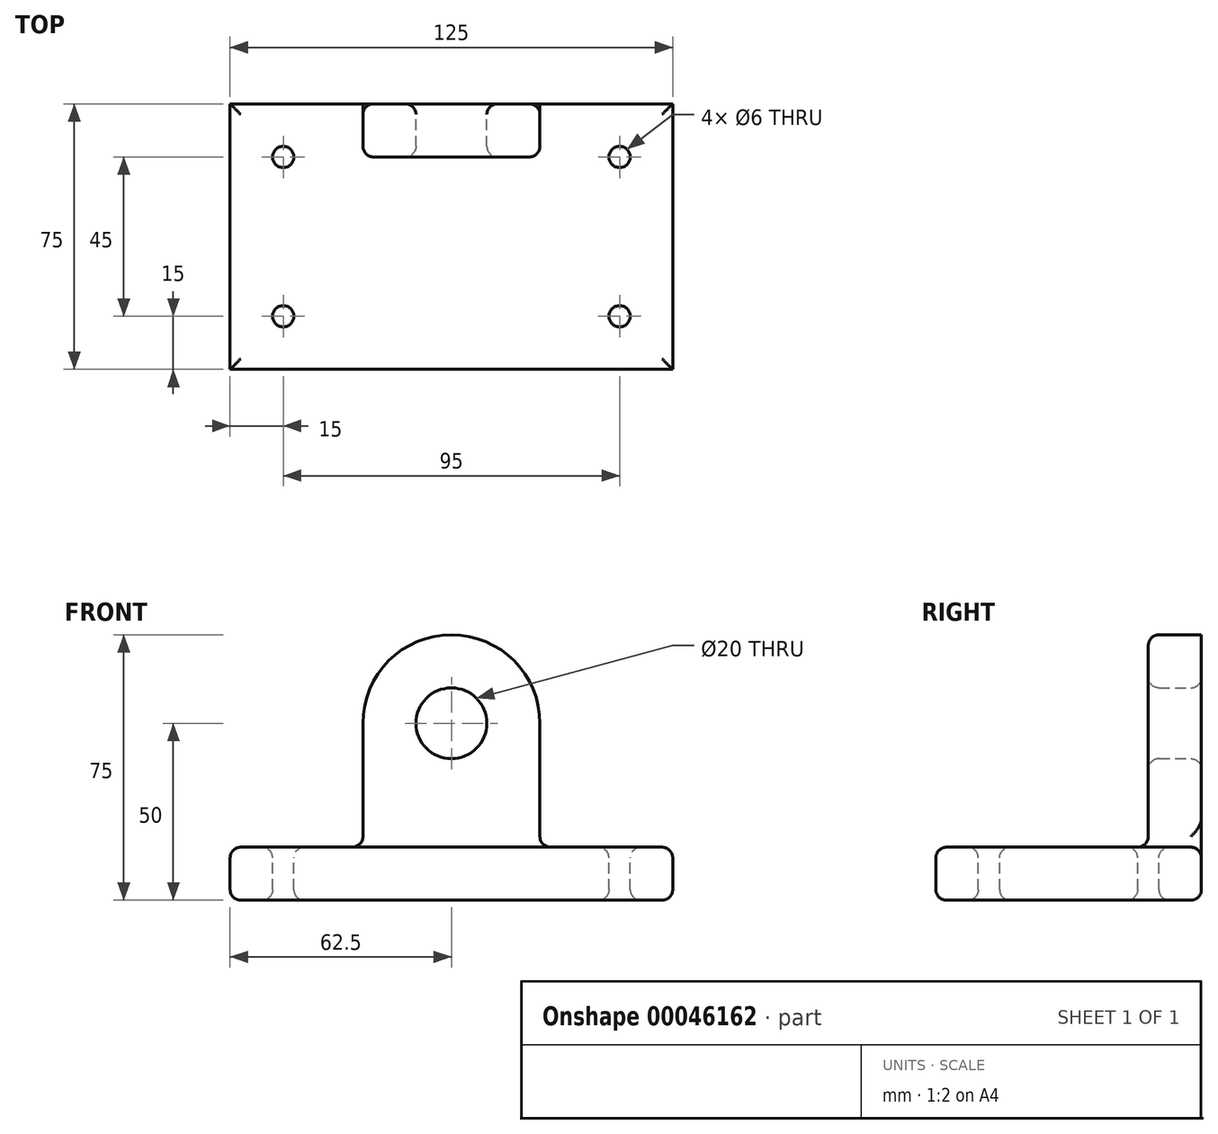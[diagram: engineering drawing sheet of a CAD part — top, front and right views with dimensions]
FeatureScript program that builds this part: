
annotation { "Feature Type Name" : "Feature", "Feature Type Description" : "" }
export const myFeature = defineFeature(function(context is Context, id is Id, definition is map)
    precondition{}
    {
        {
            var Q0;
            Q0=qCreatedBy(makeId("Top.planeOp"),FACE);
            var sketch = newSketch(context, id + "F0", { "sketchPlane" : qUnion([Q0])});
            skLineSegment(sketch, "E0.rect.bottom", {"start": v(62.5, 37.5) * mm, "end": v(-62.5, 37.5) * mm});
            skLineSegment(sketch, "E0.rect.top", {"start": v(62.5, -37.5) * mm, "end": v(-62.5, -37.5) * mm});
            skLineSegment(sketch, "E0.rect.left", {"start": v(62.5, 37.5) * mm, "end": v(62.5, -37.5) * mm});
            skLineSegment(sketch, "E0.rect.right", {"start": v(-62.5, 37.5) * mm, "end": v(-62.5, -37.5) * mm});
            skPoint(sketch, "E0.rect.middle", {"position": v(0, 0) * mm});
            skSolve(sketch);
        }
        {
            var Q0;
            Q0 = qSketchRegion(id + "F0", true);
            extrude(context, id + "F1", {"entities" : qUnion([Q0]), "depth" : 15 * mm});
        }
        {
            var Q0;
            Q0=makeQuery(id+"F1.opExtrude","SWEPT_FACE",FACE,{"disambiguationData":[OSD([sQuery(id+"F0.wireOp",EDGE,"E0.rect.bottom")])]});
            var sketch = newSketch(context, id + "F2", { "sketchPlane" : qUnion([Q0])});
            skLineSegment(sketch, "E1", {"start": v(0, 0) * mm, "end": v(0, 50) * mm, "construction": true});
            skCircle(sketch, "E2", {"center": v(0, 50) * mm, "radius": 25 * mm});
            skLineSegment(sketch, "E3.bottom", {"start": v(-25, 50) * mm, "end": v(25, 50) * mm});
            skLineSegment(sketch, "E3.top", {"start": v(-25, 0) * mm, "end": v(25, 0) * mm});
            skLineSegment(sketch, "E3.left", {"start": v(-25, 50) * mm, "end": v(-25, 0) * mm});
            skLineSegment(sketch, "E3.right", {"start": v(25, 50) * mm, "end": v(25, 0) * mm});
            skCircle(sketch, "E4", {"center": v(0, 50) * mm, "radius": 10 * mm});
            skSolve(sketch);
        }
        {
            var Q0;
            {var subQ0=sQuery(id+"F2.wireOp",EDGE,"E3.bottom");Q0=makeQuery(id+"F2.imprint","IMPRINT",FACE,{"disambiguationData":[TD([[makeQuery(id+"F2.imprint","IMPRINT",EDGE,{"derivedFrom":subQ0}),1.0]])]});}
            var Q1;
            {var subQ0=sQuery(id+"F2.wireOp",EDGE,"E3.bottom");Q1=makeQuery(id+"F2.imprint","IMPRINT",FACE,{"disambiguationData":[TD([[makeQuery(id+"F2.imprint","IMPRINT",EDGE,{"derivedFrom":subQ0}),-1.0]])]});}
            var Q2;
            {var subQ0=makeQuery(id+"F1.opExtrude","CAP_EDGE",EDGE,{"disambiguationData":[OSD([sQuery(id+"F0.wireOp",EDGE,"E0.rect.bottom")])],"isStart":false});var subQ3=sQuery(id+"F2.wireOp",EDGE,"E3.left");var subQ4=makeQuery(id+"F2.imprint","INTERSECT",VERTEX,{"derivedFrom":[subQ0,subQ3]});Q2=makeQuery(id+"F2.imprint","IMPRINT",FACE,{"disambiguationData":[TD([[makeQuery(id+"F2.imprint","IMPRINT",EDGE,{"disambiguationData":[TD([[subQ4,-1.0]])],"derivedFrom":subQ0}),1.0]])]});}
            var Q3;
            {var subQ7=sQuery(id+"F2.wireOp",EDGE,"E3.top");Q3=makeQuery(id+"F2.imprint","IMPRINT",FACE,{"disambiguationData":[TD([[makeQuery(id+"F2.imprint","IMPRINT",EDGE,{"derivedFrom":subQ7}),1.0]])]});}
            extrude(context, id + "F3", {"entities" : qUnion([Q0, Q1, Q2, Q3]), "operationType" : NewBodyOperationType.ADD, "oppositeDirection" : true, "depth" : 15 * mm});
        }
        {
            var Q0;
            Q0=makeQuery(id+"F1.opExtrude","CAP_FACE",FACE,{"disambiguationData":[OSD([sQuery(id+"F0.wireOp",EDGE,"E0.rect.bottom"),sQuery(id+"F0.wireOp",EDGE,"E0.rect.top"),sQuery(id+"F0.wireOp",EDGE,"E0.rect.left"),sQuery(id+"F0.wireOp",EDGE,"E0.rect.right")])],"isStart":false});
            var sketch = newSketch(context, id + "F4", { "sketchPlane" : qUnion([Q0])});
            skLineSegment(sketch, "E5.rect.bottom", {"start": v(-47.5, 22.5) * mm, "end": v(47.5, 22.5) * mm, "construction": true});
            skLineSegment(sketch, "E5.rect.top", {"start": v(-47.5, -22.5) * mm, "end": v(47.5, -22.5) * mm, "construction": true});
            skLineSegment(sketch, "E5.rect.left", {"start": v(-47.5, 22.5) * mm, "end": v(-47.5, -22.5) * mm, "construction": true});
            skLineSegment(sketch, "E5.rect.right", {"start": v(47.5, 22.5) * mm, "end": v(47.5, -22.5) * mm, "construction": true});
            skPoint(sketch, "E5.rect.middle", {"position": v(0, 0) * mm});
            skCircle(sketch, "E6", {"center": v(-47.5, 22.5) * mm, "radius": 3 * mm});
            skCircle(sketch, "E7", {"center": v(-47.5, -22.5) * mm, "radius": 3 * mm});
            skCircle(sketch, "E8", {"center": v(47.5, -22.5) * mm, "radius": 3 * mm});
            skCircle(sketch, "E9", {"center": v(47.5, 22.5) * mm, "radius": 3 * mm});
            skSolve(sketch);
        }
        {
            var Q0;
            Q0=makeQuery(id+"F4.imprint","IMPRINT",FACE,{"disambiguationData":[TD([[makeQuery(id+"F4.imprint","IMPRINT",EDGE,{"derivedFrom":sQuery(id+"F4.wireOp",EDGE,"E6")}),1.0]])]});
            var Q1;
            Q1=makeQuery(id+"F4.imprint","IMPRINT",FACE,{"disambiguationData":[TD([[makeQuery(id+"F4.imprint","IMPRINT",EDGE,{"derivedFrom":sQuery(id+"F4.wireOp",EDGE,"E7")}),1.0]])]});
            var Q2;
            Q2=makeQuery(id+"F4.imprint","IMPRINT",FACE,{"disambiguationData":[TD([[makeQuery(id+"F4.imprint","IMPRINT",EDGE,{"derivedFrom":sQuery(id+"F4.wireOp",EDGE,"E8")}),1.0]])]});
            var Q3;
            Q3=makeQuery(id+"F4.imprint","IMPRINT",FACE,{"disambiguationData":[TD([[makeQuery(id+"F4.imprint","IMPRINT",EDGE,{"derivedFrom":sQuery(id+"F4.wireOp",EDGE,"E9")}),1.0]])]});
            extrude(context, id + "F5", {"entities" : qUnion([Q0, Q1, Q2, Q3]), "operationType" : NewBodyOperationType.REMOVE, "oppositeDirection" : true, "depth" : 25 * mm});
        }
        {
            var Q0;
            Q0=makeQuery(id+"F3.opExtrude","CAP_FACE",FACE,{"disambiguationData":[OSD([sQuery(id+"F2.wireOp",EDGE,"E2"),sQuery(id+"F2.wireOp",EDGE,"E3.top"),sQuery(id+"F2.wireOp",EDGE,"E3.left"),sQuery(id+"F2.wireOp",EDGE,"E3.right"),sQuery(id+"F2.wireOp",EDGE,"E4")])],"isStart":false});
            var Q1;
            Q1=makeQuery(id+"F3.boolean.opBoolean","INTERSECT",EDGE,{"derivedFrom":[makeQuery(id+"F1.opExtrude","CAP_FACE",FACE,{"disambiguationData":[OSD([sQuery(id+"F0.wireOp",EDGE,"E0.rect.bottom"),sQuery(id+"F0.wireOp",EDGE,"E0.rect.top"),sQuery(id+"F0.wireOp",EDGE,"E0.rect.left"),sQuery(id+"F0.wireOp",EDGE,"E0.rect.right")])],"isStart":false}),makeQuery(id+"F3.opExtrude","CAP_FACE",FACE,{"disambiguationData":[OSD([sQuery(id+"F2.wireOp",EDGE,"E2"),sQuery(id+"F2.wireOp",EDGE,"E3.top"),sQuery(id+"F2.wireOp",EDGE,"E3.left"),sQuery(id+"F2.wireOp",EDGE,"E3.right"),sQuery(id+"F2.wireOp",EDGE,"E4")])],"isStart":false})]});
            var Q2;
            Q2=makeQuery(id+"F1.opExtrude","CAP_EDGE",EDGE,{"disambiguationData":[OSD([sQuery(id+"F0.wireOp",EDGE,"E0.rect.bottom")])],"isStart":true});
            var Q3;
            Q3=makeQuery(id+"F1.opExtrude","CAP_FACE",FACE,{"disambiguationData":[OSD([sQuery(id+"F0.wireOp",EDGE,"E0.rect.bottom"),sQuery(id+"F0.wireOp",EDGE,"E0.rect.top"),sQuery(id+"F0.wireOp",EDGE,"E0.rect.left"),sQuery(id+"F0.wireOp",EDGE,"E0.rect.right")])],"isStart":false});
            var Q4;
            Q4=makeQuery(id+"F1.opExtrude","CAP_FACE",FACE,{"disambiguationData":[OSD([sQuery(id+"F0.wireOp",EDGE,"E0.rect.bottom"),sQuery(id+"F0.wireOp",EDGE,"E0.rect.top"),sQuery(id+"F0.wireOp",EDGE,"E0.rect.left"),sQuery(id+"F0.wireOp",EDGE,"E0.rect.right")])],"isStart":true});
            var Q5;
            Q5=makeQuery(id+"F3.opExtrude","CAP_EDGE",EDGE,{"disambiguationData":[OSD([sQuery(id+"F2.wireOp",EDGE,"E4")])],"isStart":true});
            fillet(context, id + "F6", {"entities" : qUnion([Q0, Q1, Q2, Q3, Q4, Q5]), "radius" : 3 * mm, "tangentPropagation" : true, "allowEdgeOverflow" : false});
        }
    });
